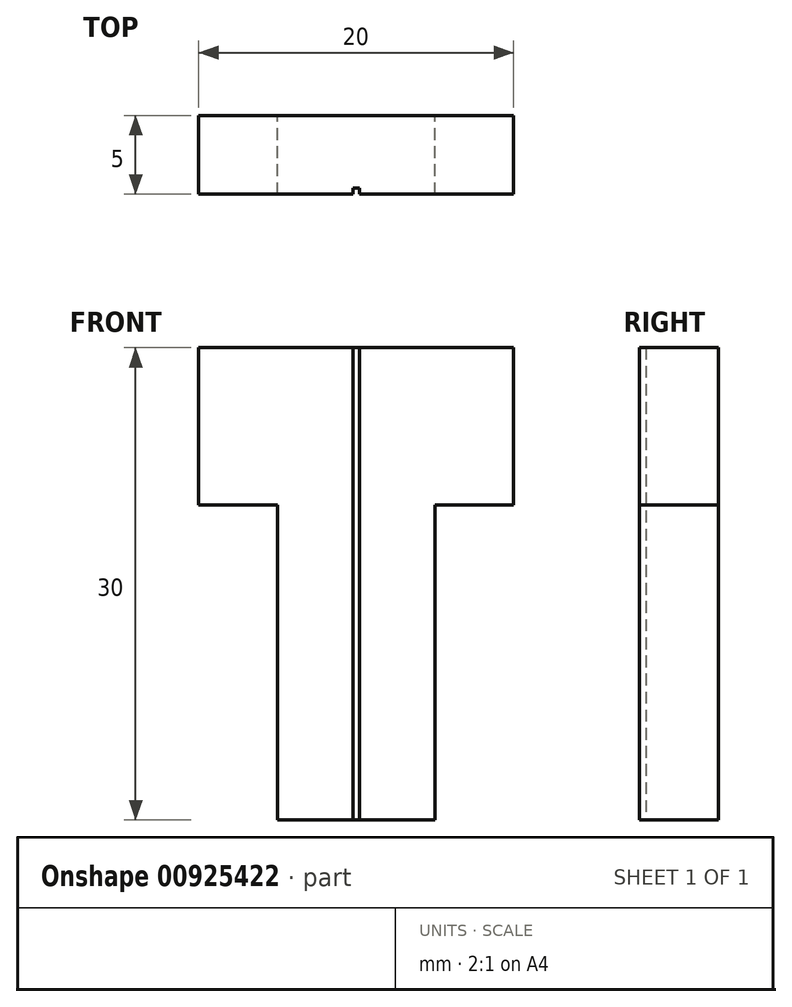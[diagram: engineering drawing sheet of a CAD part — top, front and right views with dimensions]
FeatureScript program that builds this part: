
annotation { "Feature Type Name" : "Feature", "Feature Type Description" : "" }
export const myFeature = defineFeature(function(context is Context, id is Id, definition is map)
    precondition{}
    {
        {
            var Q0;
            Q0=qCreatedBy(makeId("Front.planeOp"),FACE);
            var sketch = newSketch(context, id + "F0", { "sketchPlane" : qUnion([Q0])});
            skLineSegment(sketch, "E0.bottom", {"start": v(5, -10) * mm, "end": v(-5, -10) * mm});
            skLineSegment(sketch, "E0.left", {"start": v(5, -10) * mm, "end": v(5, 10) * mm});
            skLineSegment(sketch, "E0.right", {"start": v(-5, -10) * mm, "end": v(-5, 10) * mm});
            skPoint(sketch, "E0.middle", {"position": v(0, 0) * mm});
            skLineSegment(sketch, "E1.bottom", {"start": v(10, 10) * mm, "end": v(5, 10) * mm});
            skLineSegment(sketch, "E1.top", {"start": v(10, 20) * mm, "end": v(-10, 20) * mm});
            skLineSegment(sketch, "E1.left", {"start": v(10, 10) * mm, "end": v(10, 20) * mm});
            skLineSegment(sketch, "E1.right", {"start": v(-10, 10) * mm, "end": v(-10, 20) * mm});
            skPoint(sketch, "E1.middle", {"position": v(0, 15) * mm});
            skPoint(sketch, "E1.middle.positionSnap0", {"position": v(0, 10) * mm});
            skPoint(sketch, "E1.cornerSnap0", {"position": v(0, 10) * mm});
            skPoint(sketch, "E1.centerSnap0", {"position": v(0, 10) * mm});
            skLineSegment(sketch, "E2.trimOffspring", {"start": v(-5, 10) * mm, "end": v(-10, 10) * mm});
            skSolve(sketch);
        }
        {
            var Q0;
            Q0 = qSketchRegion(id + "F0", true);
            extrude(context, id + "F1", {"entities" : qUnion([Q0]), "depth" : 5 * mm, "offsetDistance" : 25 * mm});
        }
        {
            var Q0;
            Q0=makeQuery(id+"F1.opExtrude","CAP_FACE",FACE,{"disambiguationData":[OSD([sQuery(id+"F0.wireOp",EDGE,"E0.bottom"),sQuery(id+"F0.wireOp",EDGE,"E0.left"),sQuery(id+"F0.wireOp",EDGE,"E0.right"),sQuery(id+"F0.wireOp",EDGE,"E1.bottom"),sQuery(id+"F0.wireOp",EDGE,"E1.top"),sQuery(id+"F0.wireOp",EDGE,"E1.left"),sQuery(id+"F0.wireOp",EDGE,"E1.right"),sQuery(id+"F0.wireOp",EDGE,"E2.trimOffspring")])],"isStart":false});
            var sketch = newSketch(context, id + "F2", { "sketchPlane" : qUnion([Q0])});
            skLineSegment(sketch, "E3.bottom", {"start": v(0.2, 20) * mm, "end": v(-0.2, 20) * mm});
            skLineSegment(sketch, "E3.top", {"start": v(0.2, -20) * mm, "end": v(-0.2, -20) * mm});
            skLineSegment(sketch, "E3.left", {"start": v(0.2, 20) * mm, "end": v(0.2, -20) * mm});
            skLineSegment(sketch, "E3.right", {"start": v(-0.2, 20) * mm, "end": v(-0.2, -20) * mm});
            skPoint(sketch, "E3.middle", {"position": v(0, 0) * mm});
            skSolve(sketch);
        }
        {
            var Q0;
            Q0 = qSketchRegion(id + "F2", true);
            extrude(context, id + "F3", {"entities" : qUnion([Q0]), "operationType" : NewBodyOperationType.REMOVE, "oppositeDirection" : true, "depth" : 0.4 * mm, "offsetDistance" : 25 * mm});
        }
    });
